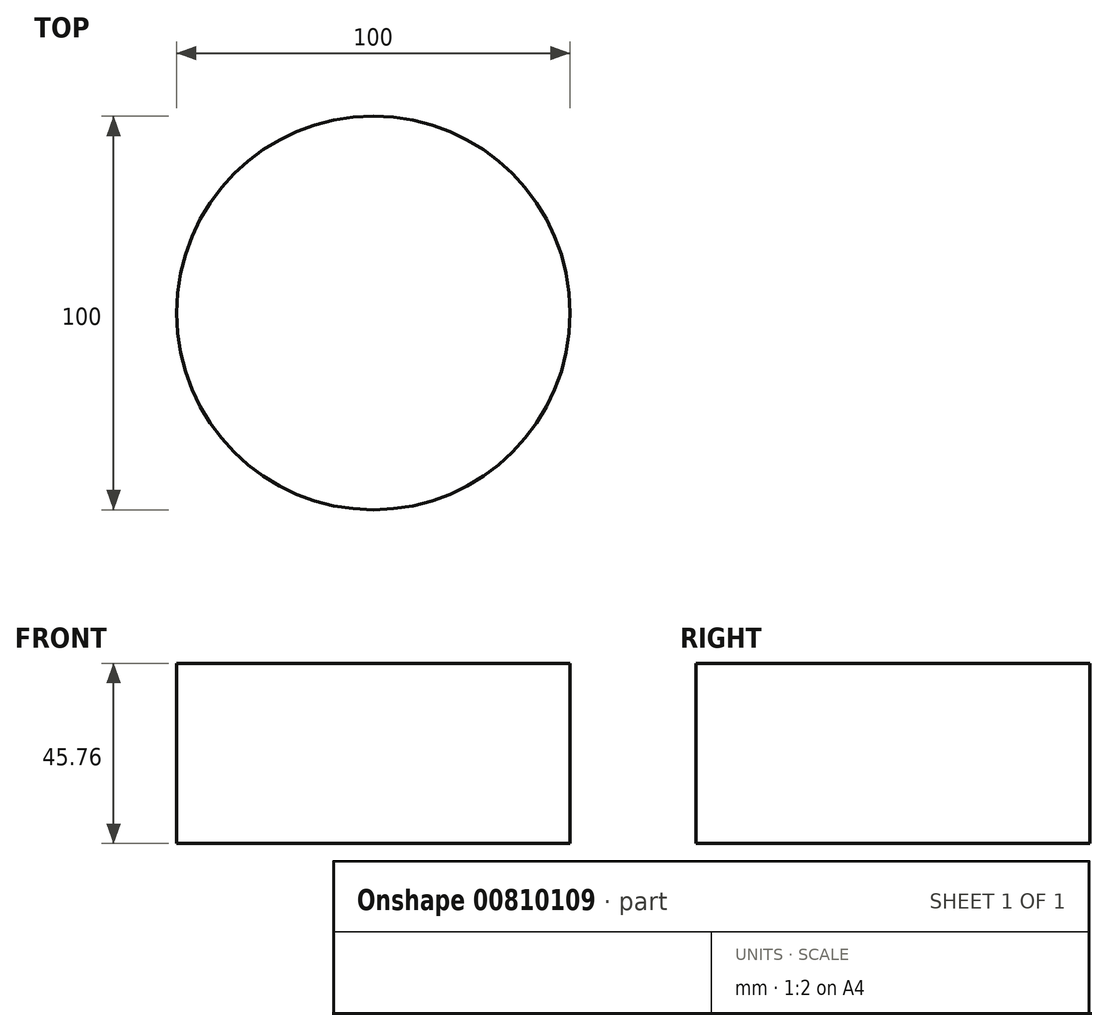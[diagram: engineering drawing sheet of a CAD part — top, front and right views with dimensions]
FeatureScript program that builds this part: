
annotation { "Feature Type Name" : "Feature", "Feature Type Description" : "" }
export const myFeature = defineFeature(function(context is Context, id is Id, definition is map)
    precondition{}
    {
        {
            var Q0;
            Q0=qCreatedBy(makeId("Top.planeOp"),FACE);
            var sketch = newSketch(context, id + "F0", { "sketchPlane" : qUnion([Q0])});
            skCircle(sketch, "E0", {"center": v(0, 0) * mm, "radius": 50 * mm});
            skSolve(sketch);
        }
        {
            var Q0;
            Q0=qCreatedBy(makeId("Front.planeOp"),FACE);
            var sketch = newSketch(context, id + "F1", { "sketchPlane" : qUnion([Q0])});
            skLineSegment(sketch, "E1", {"start": v(0, 0) * mm, "end": v(0, 45.76) * mm});
            skSolve(sketch);
        }
        {
            var Q0;
            Q0=makeQuery(id+"F0.imprint","IMPRINT",FACE,{"disambiguationData":[TD([[makeQuery(id+"F0.imprint","IMPRINT",EDGE,{"derivedFrom":sQuery(id+"F0.wireOp",EDGE,"E0")}),1.0]])]});
            var Q1;
            Q1 = qBodyType(qCreatedBy(id + "F0" ,EDGE), BodyType.WIRE);
            var Q2;
            Q2=sQuery(id+"F1.wireOp",EDGE,"E1");
            sweep(context, id + "F2", {"profiles" : qUnion([Q0]), "surfaceProfiles" : qUnion([Q1]), "path" : qUnion([Q2]), "keepProfileOrientation" : true});
        }
    });
